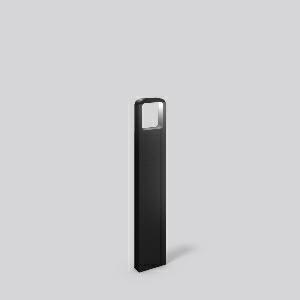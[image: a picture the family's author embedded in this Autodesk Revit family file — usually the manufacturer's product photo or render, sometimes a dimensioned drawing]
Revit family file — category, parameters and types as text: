
# Revit family: hb_203_611976_0031_f2f5
name_source: partatom
category: Lighting Fixtures
units: mm (PartAtom-declared; Revit-internal decimal feet)

## family parameters
Cut with Voids When Loaded = No
Host = Face
Light Source = No
Part Type = Normal
Room Calculation Point = No
Round Connector Dimension = Use Diameter
Shared = No

## types (1)
- HB 203 (1 x LED Modul 830, 290 lm, 3000)
    Apparent Load = 9 VA
    CIE Flux Codes = 44 77 95 99 100
    Color Rendering = 80
    Color Temperature = 3000
    Default Elevation = 1800 mm
    Description = Series: HB 203
Bollard for socket mounting. Housing: die-cast aluminium, powder-coated. Diffuser: plastic (polycarbonate), opal. Driver integrated. 
Colour: anthracite metallic (DB703)
Length: 40 mm
Width: 120 mm
Height: 650 mm
Lamp: LED
System power: 9 W
Rated luminous flux: 290 lm
Luminous efficiency: 32 lm/W
Control gear: Regulated power supply
Protection class: I
Type of protection: IP 54
    Height = 650 mm
    Lamp = 1 x LED Modul 830
    Lamp Light Flux = 290 lm
    Lamp count = 1
    Length = 40 mm
    Lifetime = 50000 h
    Luminous efficacy = 32 lm/W
    Manufacturer = RZB
    ModVariant = No
    Model = 611976.0031
    Mounting Place = Floor
    Mounting Type = Freestanding
    Number of Poles = 1
    OnlyDefault = Yes
    Power Factor = 1
    Product Name = HB 203
    Product group = Bollards
    ProductGroupID = 1351
    Protection Class = Protection class I
    Protection Degree = IP 54
    RLX_Detail_Level = 1
    RLX_Emergency_Light_Flux = 0 lm
    RLX_Emergency_Type = 0
    RLX_Emergency_Type_DB = No
    RlxData = <blob elided: 23969 chars, md5=c2d079c9>
    Socket = socket
    Standby Power = 0 W
    System Light Flux = 290 lm
    System Power = 9 W
    Type Comments = Product without accessories
    Type Image = 611976.0031.jpg
    URL = http://relux.com
    VarID = ---
    Voltage = 0 V
    Weight = 0.00 kg
    Width = 120 mm

## geometry (parser evidence)
native form markers: Blend x4, Sweep x11
no freeform markers — native parametric forms only
